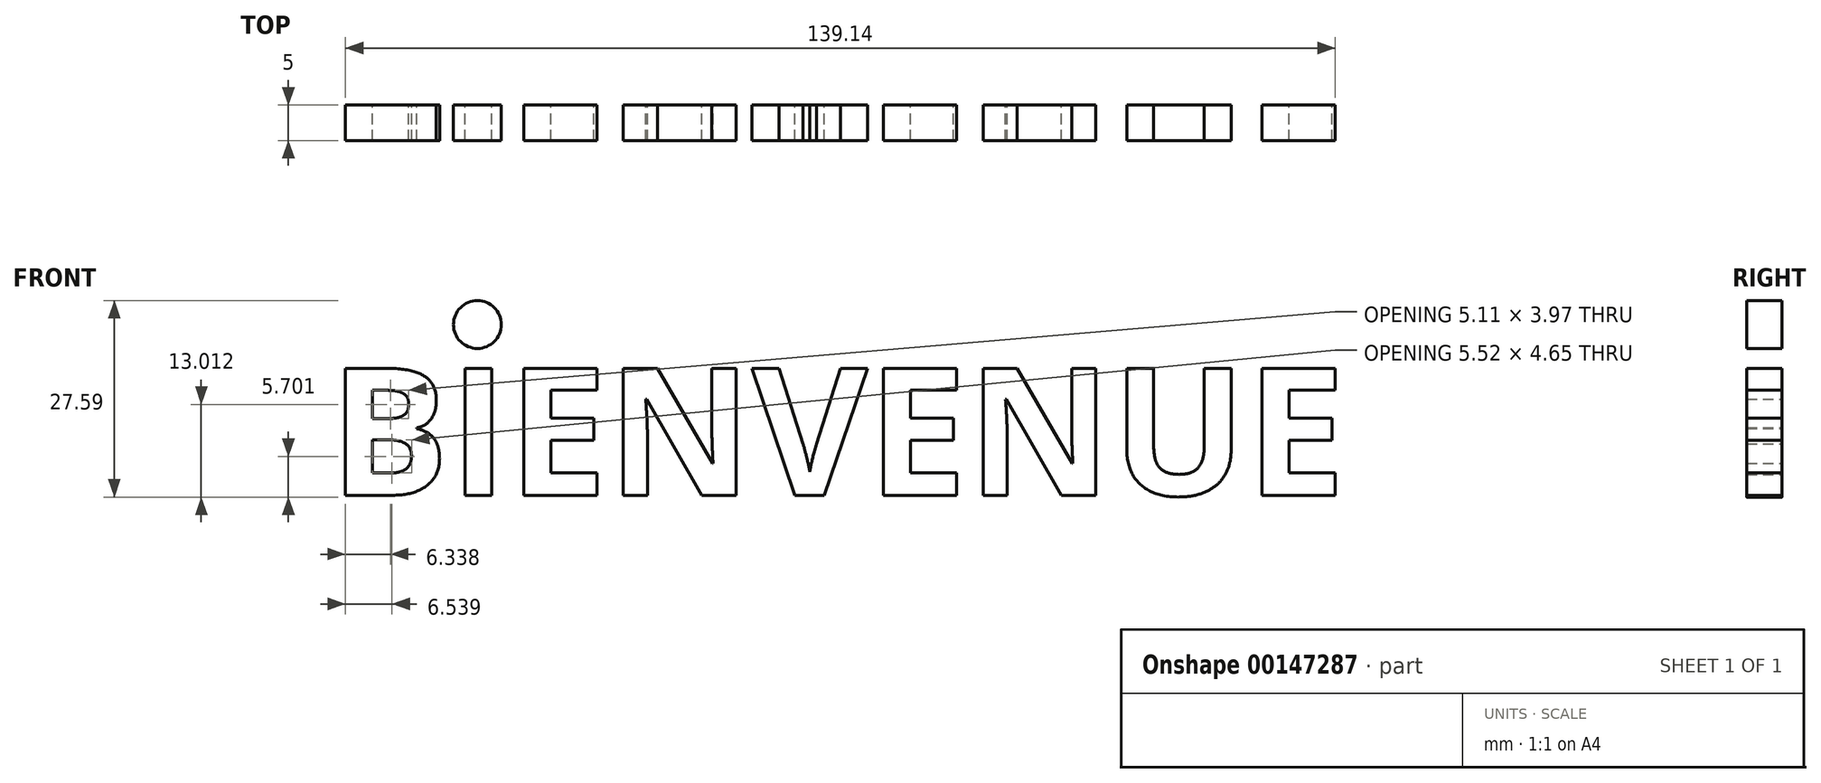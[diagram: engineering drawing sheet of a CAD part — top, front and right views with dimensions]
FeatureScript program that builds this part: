
annotation { "Feature Type Name" : "Feature", "Feature Type Description" : "" }
export const myFeature = defineFeature(function(context is Context, id is Id, definition is map)
    precondition{}
    {
        {
            var Q0;
            Q0=qCreatedBy(makeId("Front.planeOp"),FACE);
            var sketch = newSketch(context, id + "F0", { "sketchPlane" : qUnion([Q0])});
            skText(sketch, "E0", { "text": "BIENVENUE", "fontName": "OpenSans-Bold.ttf"});
            skCircle(sketch, "E1", {"center": v(-50.7, 23.98) * mm, "radius": 3.36 * mm});
            const initialGuessF0  = {"E0": [-0.0715, 0, 1, 0, 0.018]};
            skSetInitialGuess(sketch, initialGuessF0);
            skSolve(sketch);
        }
        {
            var Q0;
            Q0 = qSketchRegion(id + "F0", true);
            extrude(context, id + "F1", {"entities" : qUnion([Q0]), "depth" : 5 * mm});
        }
    });
